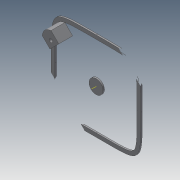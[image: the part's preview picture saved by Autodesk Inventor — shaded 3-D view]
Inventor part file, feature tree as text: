
AUTODESK INVENTOR PART (.ipt)
format: ipt  version: 2014 SP1 (Build 180222100, 222)  size: 244,224 bytes
history: native  units: in
note: dims shown in document units (in); Inventor stores cm internally (conversion verified against a paired STEP export)
features: extrude x3, sketch x3, other x1, pattern_circular x1
ambient origin geometry x8: Origin, YZ Plane, XZ Plane, XY Plane, X Axis, Y Axis, Z Axis, Center Point
bodies: Solid1 (feature_tree)
feature tree (8):
  extrude  "Extrusion1"  Depth=0.27in
  other  "Work Axis1"
  extrude  "Extrusion2"  Depth=0.11in
  extrude  "Extrusion3"  Depth=0.8in
  pattern_circular  "Circular Pattern1"  [2 undecoded]
  sketch  "Sketch1"  dims[d0=2.6in d1=2.5998in d2=3.25in d3=0.27in]
  sketch  "Sketch2"  dims[d4=0.11in d5=0.0in d6=1.0in]
  sketch  "Sketch3"  dims[d7=4.5in d8=4.5in d9=2.25in d10=2.25in d11=0.25in d12=0.35in d13=0.45in d14=0.45in d15=1.0in d16=0.0in d17=1.0in d18=0.8in d19=0.0in d20=1.5748in d21=360.0deg]
note: 2 required parameter values undecoded (feature->parameter linkage not recoverable at this tier; creation-order binding heuristic only, values carry confidence <= 0.55)
